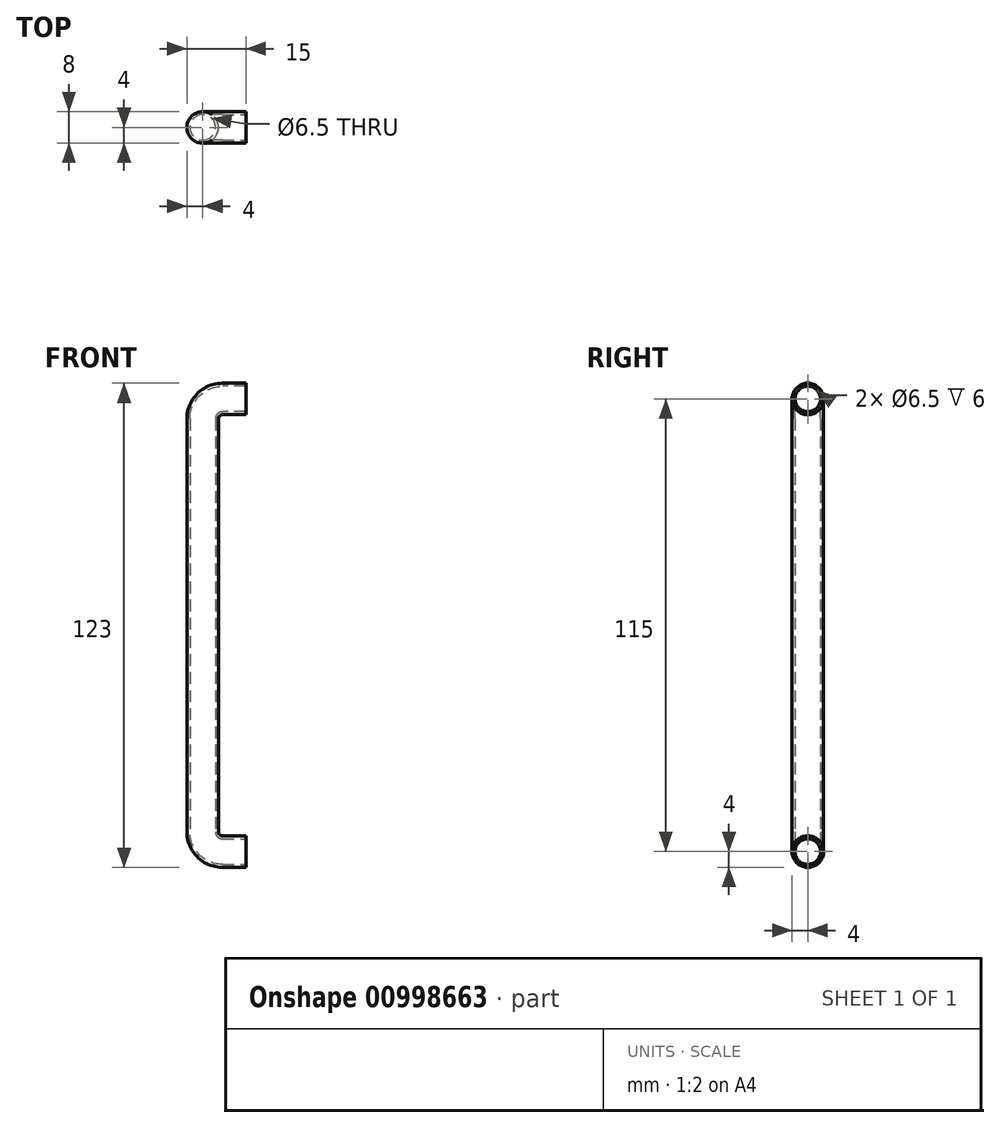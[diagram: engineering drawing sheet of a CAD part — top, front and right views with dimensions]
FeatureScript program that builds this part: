
annotation { "Feature Type Name" : "Feature", "Feature Type Description" : "" }
export const myFeature = defineFeature(function(context is Context, id is Id, definition is map)
    precondition{}
    {
        {
            var Q0;
            Q0=qCreatedBy(makeId("Right.planeOp"),FACE);
            var sketch = newSketch(context, id + "F0", { "sketchPlane" : qUnion([Q0])});
            skCircle(sketch, "E0", {"center": v(0, 0) * mm, "radius": 4 * mm});
            skCircle(sketch, "E1", {"center": v(0, 0) * mm, "radius": 3.25 * mm});
            skSolve(sketch);
        }
        {
            var Q0;
            Q0=qCreatedBy(makeId("Front.planeOp"),FACE);
            var sketch = newSketch(context, id + "F1", { "sketchPlane" : qUnion([Q0])});
            skLineSegment(sketch, "E2", {"start": v(0, 0) * mm, "end": v(-6, 0) * mm});
            skLineSegment(sketch, "E3", {"start": v(-11, -5) * mm, "end": v(-11, -110) * mm});
            skPoint(sketch, "E4.visualSharp", {"position": v(-11, 0) * mm});
            skArc(sketch, "E4.filletArc", {"start": v(-6, 0) * mm, "mid": v(-9.54, -1.46) * mm, "end": v(-11, -5) * mm});
            skLineSegment(sketch, "E5", {"start": v(-6, -115) * mm, "end": v(0, -115) * mm});
            skPoint(sketch, "E6.visualSharp", {"position": v(-11, -115) * mm});
            skArc(sketch, "E6.filletArc", {"start": v(-11, -110) * mm, "mid": v(-9.54, -113.54) * mm, "end": v(-6, -115) * mm});
            skSolve(sketch);
        }
        {
            var Q0;
            Q0=qSketchRegion(id+"F0",true);
            var Q1;
            Q1=qConstructionFilter(qBodyType(qCreatedBy(id+"F1",EDGE),BodyType.WIRE),ConstructionObject.NO);
            sweep(context, id + "F2", {"profiles" : qUnion([Q0]), "path" : qUnion([Q1])});
        }
    });
